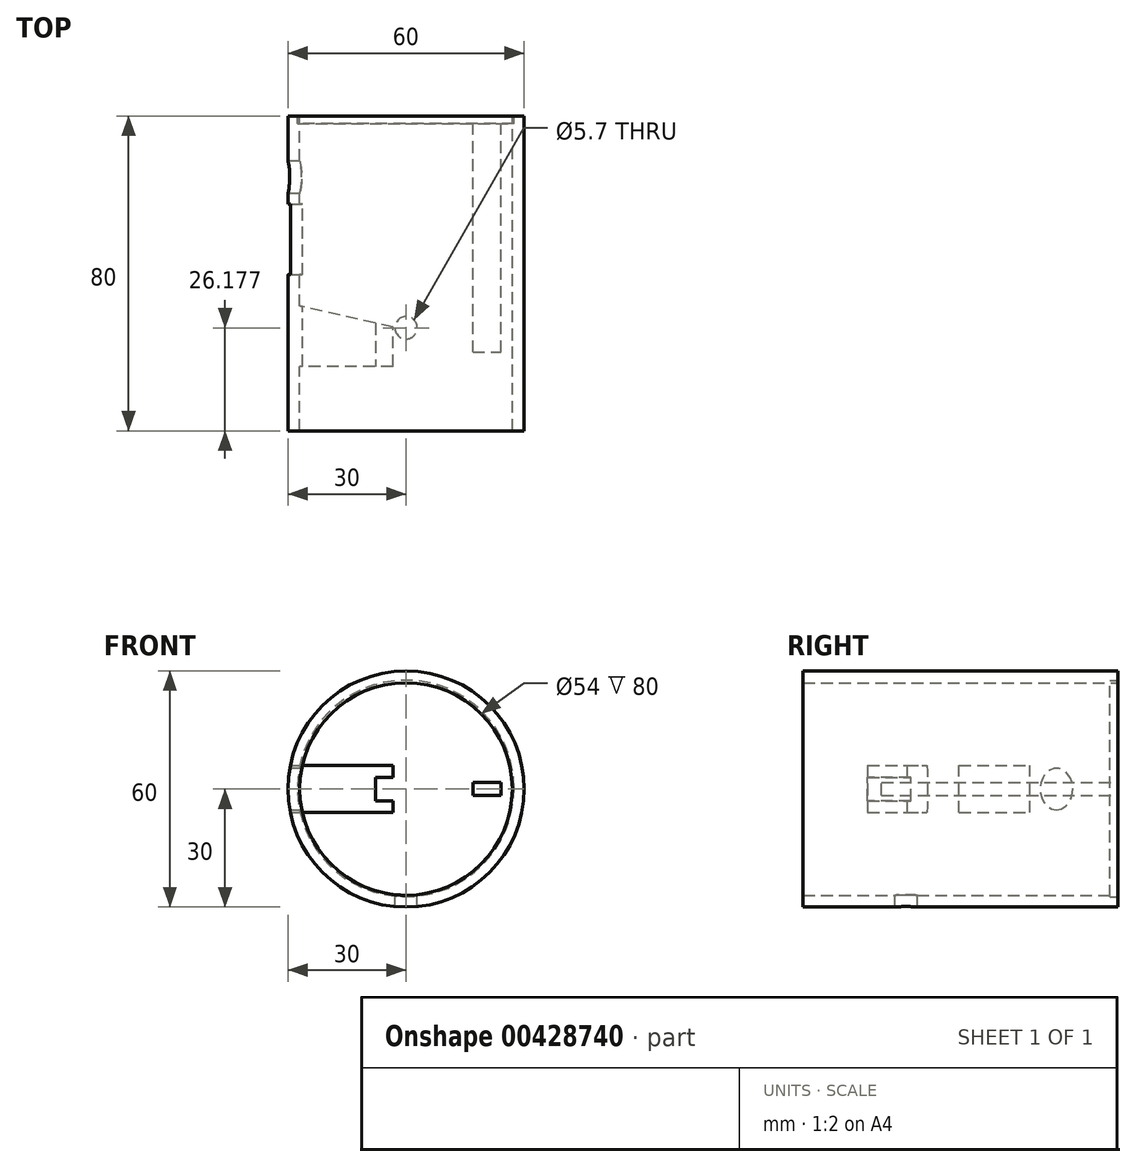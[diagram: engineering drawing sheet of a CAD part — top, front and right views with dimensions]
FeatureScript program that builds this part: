
annotation { "Feature Type Name" : "Feature", "Feature Type Description" : "" }
export const myFeature = defineFeature(function(context is Context, id is Id, definition is map)
    precondition{}
    {
        {
            var Q0;
            Q0=qCreatedBy(makeId("Front.planeOp"),FACE);
            var sketch = newSketch(context, id + "F0", { "sketchPlane" : qUnion([Q0])});
            skCircle(sketch, "E0", {"center": v(0, 0) * mm, "radius": 30 * mm});
            skCircle(sketch, "E1", {"center": v(0, 0) * mm, "radius": 27 * mm});
            skLineSegment(sketch, "E2.bottom", {"start": v(17, 0) * mm, "end": v(27, 0) * mm});
            skLineSegment(sketch, "E2.top", {"start": v(17, -6) * mm, "end": v(26.32, -6) * mm});
            skLineSegment(sketch, "E2.left", {"start": v(17, 0) * mm, "end": v(17, -6) * mm});
            skLineSegment(sketch, "E3.MirrorCS", {"start": v(17, 0) * mm, "end": v(17, 6) * mm});
            skLineSegment(sketch, "E4.MirrorCS", {"start": v(17, 6) * mm, "end": v(26.32, 6) * mm});
            skLineSegment(sketch, "E5.bottom", {"start": v(17, 0) * mm, "end": v(24.16, 0) * mm});
            skLineSegment(sketch, "E5.top", {"start": v(17, -1.62) * mm, "end": v(24.16, -1.62) * mm});
            skLineSegment(sketch, "E5.left", {"start": v(17, 0) * mm, "end": v(17, -1.62) * mm});
            skLineSegment(sketch, "E5.right", {"start": v(24.16, 0) * mm, "end": v(24.16, -1.62) * mm});
            skLineSegment(sketch, "E6.MirrorCS", {"start": v(17, 1.62) * mm, "end": v(24.16, 1.62) * mm});
            skLineSegment(sketch, "E7.MirrorCS", {"start": v(24.16, 0) * mm, "end": v(24.16, 1.62) * mm});
            skSolve(sketch);
        }
        {
            var Q0;
            Q0=makeQuery(id+"F0.imprint","IMPRINT",FACE,{"disambiguationData":[TD([[makeQuery(id+"F0.imprint","IMPRINT",EDGE,{"derivedFrom":sQuery(id+"F0.wireOp",EDGE,"E0")}),1.0]])]});
            extrude(context, id + "F1", {"entities" : qUnion([Q0]), "depth" : 80 * mm});
        }
        {
            var Q0;
            Q0=qCreatedBy(makeId("Front.planeOp"),FACE);
            var sketch = newSketch(context, id + "F2", { "sketchPlane" : qUnion([Q0])});
            skCircle(sketch, "E8", {"center": v(-0.08, 0.14) * mm, "radius": 27.5 * mm});
            skSolve(sketch);
        }
        {
            var Q0;
            Q0=qSketchRegion(id+"F2",true);
            extrude(context, id + "F3", {"entities" : qUnion([Q0]), "depth" : 2 * mm});
        }
        {
            var Q0;
            Q0=qCreatedBy(makeId("Top.planeOp"),FACE);
            var sketch = newSketch(context, id + "F4", { "sketchPlane" : qUnion([Q0])});
            skLineSegment(sketch, "E9.bottom", {"start": v(-32.36, -22.34) * mm, "end": v(-18.81, -22.34) * mm});
            skLineSegment(sketch, "E9.top", {"start": v(-32.36, -40.34) * mm, "end": v(-18.81, -40.34) * mm});
            skLineSegment(sketch, "E9.left", {"start": v(-32.36, -22.34) * mm, "end": v(-32.36, -40.34) * mm});
            skLineSegment(sketch, "E9.right", {"start": v(-18.81, -22.34) * mm, "end": v(-18.81, -40.34) * mm});
            skSolve(sketch);
        }
        {
            var Q0;
            Q0=makeQuery(id+"F4.imprint","IMPRINT",FACE,{"disambiguationData":[TD([[makeQuery(id+"F4.imprint","IMPRINT",EDGE,{"derivedFrom":sQuery(id+"F4.wireOp",EDGE,"E9.bottom")}),-1.0]])]});
            var Q1;
            Q1 = qSketchRegion(id + "F6", true);
            extrude(context, id + "F5", {"entities" : qUnion([Q0, Q1]), "operationType" : NewBodyOperationType.REMOVE, "endBound" : BoundingType.SYMMETRIC, "depth" : 12 * mm, "hasSecondDirection" : true, "secondDirectionOppositeDirection" : true, "secondDirectionDepth" : 4.6 * mm});
        }
        {
            var Q0;
            Q0=qCreatedBy(makeId("Top.planeOp"),FACE);
            var sketch = newSketch(context, id + "F6", { "sketchPlane" : qUnion([Q0])});
            skCircle(sketch, "E10", {"center": v(0, -53.82) * mm, "radius": 2.85 * mm});
            skSolve(sketch);
        }
        {
            var Q0;
            Q0=makeQuery(id+"F6.imprint","IMPRINT",FACE,{"disambiguationData":[TD([[makeQuery(id+"F6.imprint","IMPRINT",EDGE,{"derivedFrom":sQuery(id+"F6.wireOp",EDGE,"E10")}),1.0]])]});
            var Q1;
            Q1=sQuery(id+"F6.wireOp",EDGE,"E10");
            extrude(context, id + "F7", {"entities" : qUnion([Q0]), "operationType" : NewBodyOperationType.REMOVE, "surfaceEntities" : qUnion([Q1]), "oppositeDirection" : true, "depth" : 34.4 * mm});
        }
        {
            var Q0;
            Q0=qCreatedBy(makeId("Top.planeOp"),FACE);
            var sketch = newSketch(context, id + "F8", { "sketchPlane" : qUnion([Q0])});
            skLineSegment(sketch, "E11.bottom", {"start": v(-3.31, -63.62) * mm, "end": v(-27.31, -63.62) * mm});
            skLineSegment(sketch, "E11.top", {"start": v(-3.31, -53.62) * mm, "end": v(-27.31, -53.62) * mm});
            skLineSegment(sketch, "E11.left", {"start": v(-3.31, -63.62) * mm, "end": v(-3.31, -53.62) * mm});
            skLineSegment(sketch, "E11.right", {"start": v(-27.31, -63.62) * mm, "end": v(-27.31, -53.62) * mm});
            skLineSegment(sketch, "E12", {"start": v(-3.31, -53.62) * mm, "end": v(-27.46, -48.22) * mm});
            skLineSegment(sketch, "E13", {"start": v(-27.46, -48.22) * mm, "end": v(-27.31, -53.62) * mm});
            skSolve(sketch);
        }
        {
            var Q0;
            Q0=makeQuery(id+"F8.imprint","IMPRINT",FACE,{"disambiguationData":[TD([[makeQuery(id+"F8.imprint","IMPRINT",EDGE,{"derivedFrom":sQuery(id+"F8.wireOp",EDGE,"E11.top")}),-1.0]])]});
            extrude(context, id + "F9", {"entities" : qUnion([Q0]), "operationType" : NewBodyOperationType.ADD, "endBound" : BoundingType.SYMMETRIC, "depth" : 12 * mm});
        }
        {
            var Q0;
            Q0=makeQuery(id+"F8.imprint","IMPRINT",FACE,{"disambiguationData":[TD([[makeQuery(id+"F8.imprint","IMPRINT",EDGE,{"derivedFrom":sQuery(id+"F8.wireOp",EDGE,"E11.bottom")}),-1.0]])]});
            extrude(context, id + "F10", {"entities" : qUnion([Q0]), "operationType" : NewBodyOperationType.ADD, "endBound" : BoundingType.SYMMETRIC, "depth" : 12 * mm});
        }
        {
            var Q0;
            Q0=qCreatedBy(makeId("Top.planeOp"),FACE);
            var sketch = newSketch(context, id + "F11", { "sketchPlane" : qUnion([Q0])});
            skLineSegment(sketch, "E14.bottom", {"start": v(-7.77, -49.01) * mm, "end": v(-2.6, -49.01) * mm});
            skLineSegment(sketch, "E14.top", {"start": v(-7.77, -67.01) * mm, "end": v(-2.6, -67.01) * mm});
            skLineSegment(sketch, "E14.left", {"start": v(-7.77, -49.01) * mm, "end": v(-7.77, -67.01) * mm});
            skLineSegment(sketch, "E14.right", {"start": v(-2.6, -49.01) * mm, "end": v(-2.6, -67.01) * mm});
            skSolve(sketch);
        }
        {
            var Q0;
            Q0=qSketchRegion(id+"F11",true);
            extrude(context, id + "F12", {"entities" : qUnion([Q0]), "operationType" : NewBodyOperationType.REMOVE, "endBound" : BoundingType.SYMMETRIC, "depth" : 6 * mm});
        }
        {
            var Q0;
            {var subQ1=sQuery(id+"F0.wireOp",EDGE,"E2.bottom");Q0=makeQuery(id+"F0.imprint","IMPRINT",FACE,{"disambiguationData":[TD([[makeQuery(id+"F0.imprint","IMPRINT",EDGE,{"derivedFrom":subQ1}),1.0]])]});}
            var Q1;
            {var subQ1=sQuery(id+"F0.wireOp",EDGE,"E2.bottom");Q1=makeQuery(id+"F0.imprint","IMPRINT",FACE,{"disambiguationData":[TD([[makeQuery(id+"F0.imprint","IMPRINT",EDGE,{"derivedFrom":subQ1}),-1.0]])]});}
            extrude(context, id + "F13", {"entities" : qUnion([Q0, Q1]), "depth" : 60 * mm});
        }
        {
            var Q0;
            Q0=qCreatedBy(makeId("Right.planeOp"),FACE);
            var sketch = newSketch(context, id + "F14", { "sketchPlane" : qUnion([Q0])});
            skEllipse(sketch, "E15", {"center": v(-15.58, 0) * mm, "majorRadius": 5.25 * mm, "minorRadius": 4.16 * mm, "majorAxis": v(0, -1)});
            skSolve(sketch);
        }
        {
            var Q0;
            Q0 = qSketchRegion(id + "F14", true);
            extrude(context, id + "F15", {"entities" : qUnion([Q0]), "operationType" : NewBodyOperationType.REMOVE, "oppositeDirection" : true, "depth" : 50 * mm});
        }
    });
